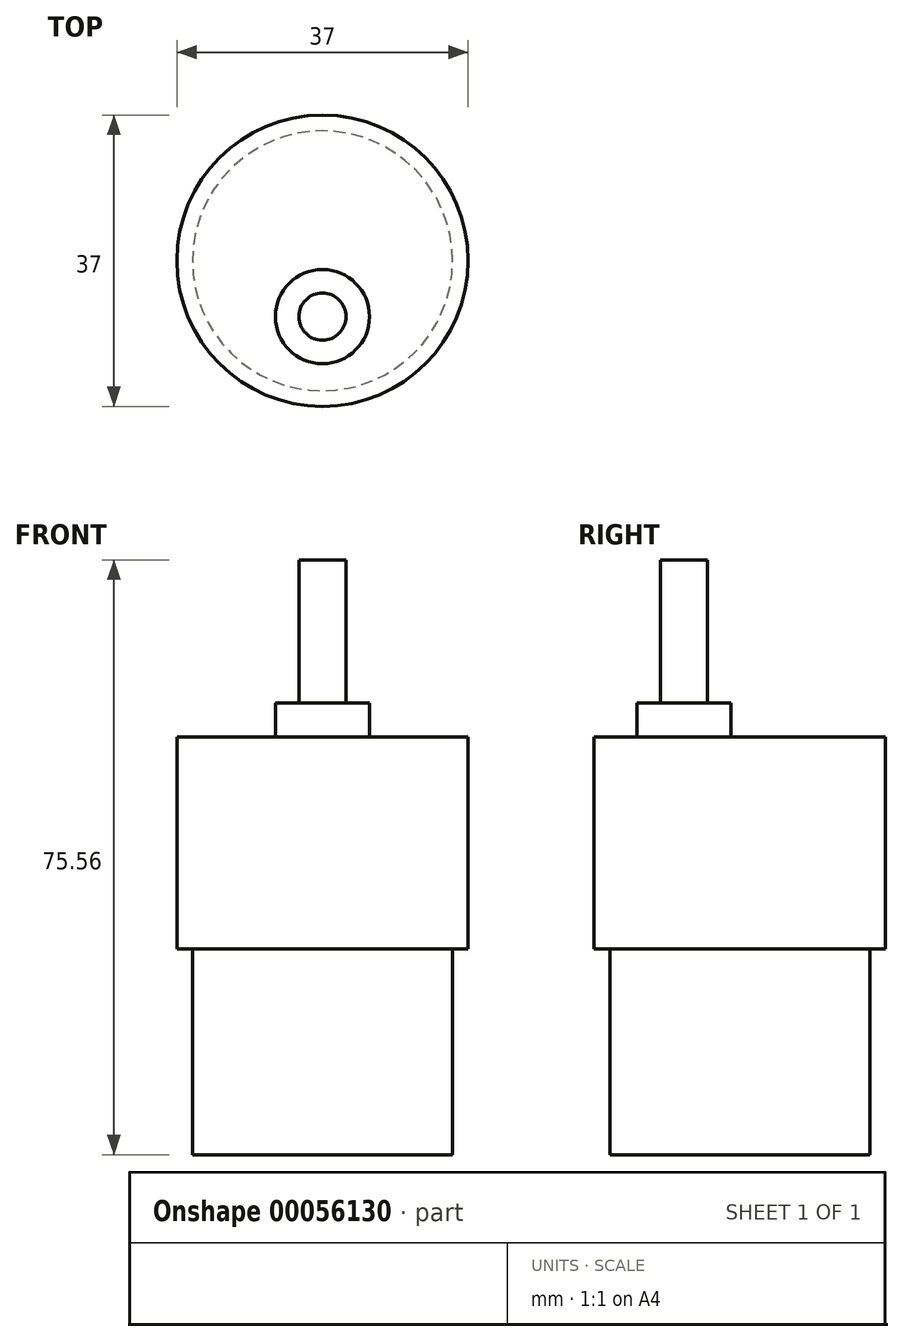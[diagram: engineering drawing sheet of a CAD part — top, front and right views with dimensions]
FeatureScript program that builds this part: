
annotation { "Feature Type Name" : "Feature", "Feature Type Description" : "" }
export const myFeature = defineFeature(function(context is Context, id is Id, definition is map)
    precondition{}
    {
        {
            var Q0;
            Q0=qCreatedBy(makeId("Top.planeOp"),FACE);
            var sketch = newSketch(context, id + "F0", { "sketchPlane" : qUnion([Q0])});
            skCircle(sketch, "E0", {"center": v(0, 0) * mm, "radius": 18.5 * mm});
            skSolve(sketch);
        }
        {
            var Q0;
            Q0=makeQuery(id+"F0.imprint","IMPRINT",FACE,{"disambiguationData":[TD([[makeQuery(id+"F0.imprint","IMPRINT",EDGE,{"derivedFrom":sQuery(id+"F0.wireOp",EDGE,"E0")}),1.0]])]});
            var Q1;
            Q1=sQuery(id+"F0.wireOp",EDGE,"E0");
            extrude(context, id + "F1", {"entities" : qUnion([Q0]), "surfaceEntities" : qUnion([Q1]), "depth" : 26.92 * mm});
        }
        {
            var Q0;
            Q0=makeQuery(id+"F1.opExtrude","CAP_FACE",FACE,{"disambiguationData":[OSD([sQuery(id+"F0.wireOp",EDGE,"E0")])],"isStart":true});
            var sketch = newSketch(context, id + "F2", { "sketchPlane" : qUnion([Q0])});
            skCircle(sketch, "E1", {"center": v(0, 0) * mm, "radius": 16.51 * mm});
            skSolve(sketch);
        }
        {
            var Q0;
            Q0=makeQuery(id+"F2.imprint","IMPRINT",FACE,{"disambiguationData":[TD([[makeQuery(id+"F2.imprint","IMPRINT",EDGE,{"derivedFrom":sQuery(id+"F2.wireOp",EDGE,"E1")}),1.0]])]});
            var Q1;
            Q1=sQuery(id+"F2.wireOp",EDGE,"E1");
            extrude(context, id + "F3", {"entities" : qUnion([Q0]), "operationType" : NewBodyOperationType.ADD, "surfaceEntities" : qUnion([Q1]), "depth" : 26.16 * mm});
        }
        {
            var Q0;
            Q0=makeQuery(id+"F1.opExtrude","CAP_FACE",FACE,{"disambiguationData":[OSD([sQuery(id+"F0.wireOp",EDGE,"E0")])],"isStart":false});
            var sketch = newSketch(context, id + "F4", { "sketchPlane" : qUnion([Q0])});
            skCircle(sketch, "E2.0", {"center": v(0, 0) * mm, "radius": 18.5 * mm});
            skLineSegment(sketch, "E3", {"start": v(0, -18.5) * mm, "end": v(0, -7.1) * mm});
            skCircle(sketch, "E4", {"center": v(0, -7.1) * mm, "radius": 5.97 * mm});
            skSolve(sketch);
        }
        {
            var Q0;
            Q0=makeQuery(id+"F4.imprint","IMPRINT",FACE,{"disambiguationData":[TD([[makeQuery(id+"F4.imprint","IMPRINT",EDGE,{"derivedFrom":sQuery(id+"F4.wireOp",EDGE,"E4")}),1.0]])]});
            extrude(context, id + "F5", {"entities" : qUnion([Q0]), "operationType" : NewBodyOperationType.ADD, "depth" : 4.32 * mm});
        }
        {
            var Q0;
            Q0=makeQuery(id+"F5.opExtrude","CAP_FACE",FACE,{"disambiguationData":[OSD([sQuery(id+"F4.wireOp",EDGE,"E4")])],"isStart":false});
            var sketch = newSketch(context, id + "F6", { "sketchPlane" : qUnion([Q0])});
            skCircle(sketch, "E5", {"center": v(0, -7.1) * mm, "radius": 3 * mm});
            skSolve(sketch);
        }
        {
            var Q0;
            Q0=makeQuery(id+"F6.imprint","IMPRINT",FACE,{"disambiguationData":[TD([[makeQuery(id+"F6.imprint","IMPRINT",EDGE,{"derivedFrom":sQuery(id+"F6.wireOp",EDGE,"E5")}),1.0]])]});
            var Q1;
            Q1=sQuery(id+"F6.wireOp",EDGE,"E5");
            extrude(context, id + "F7", {"entities" : qUnion([Q0]), "operationType" : NewBodyOperationType.ADD, "surfaceEntities" : qUnion([Q1]), "depth" : 18.16 * mm});
        }
    });
